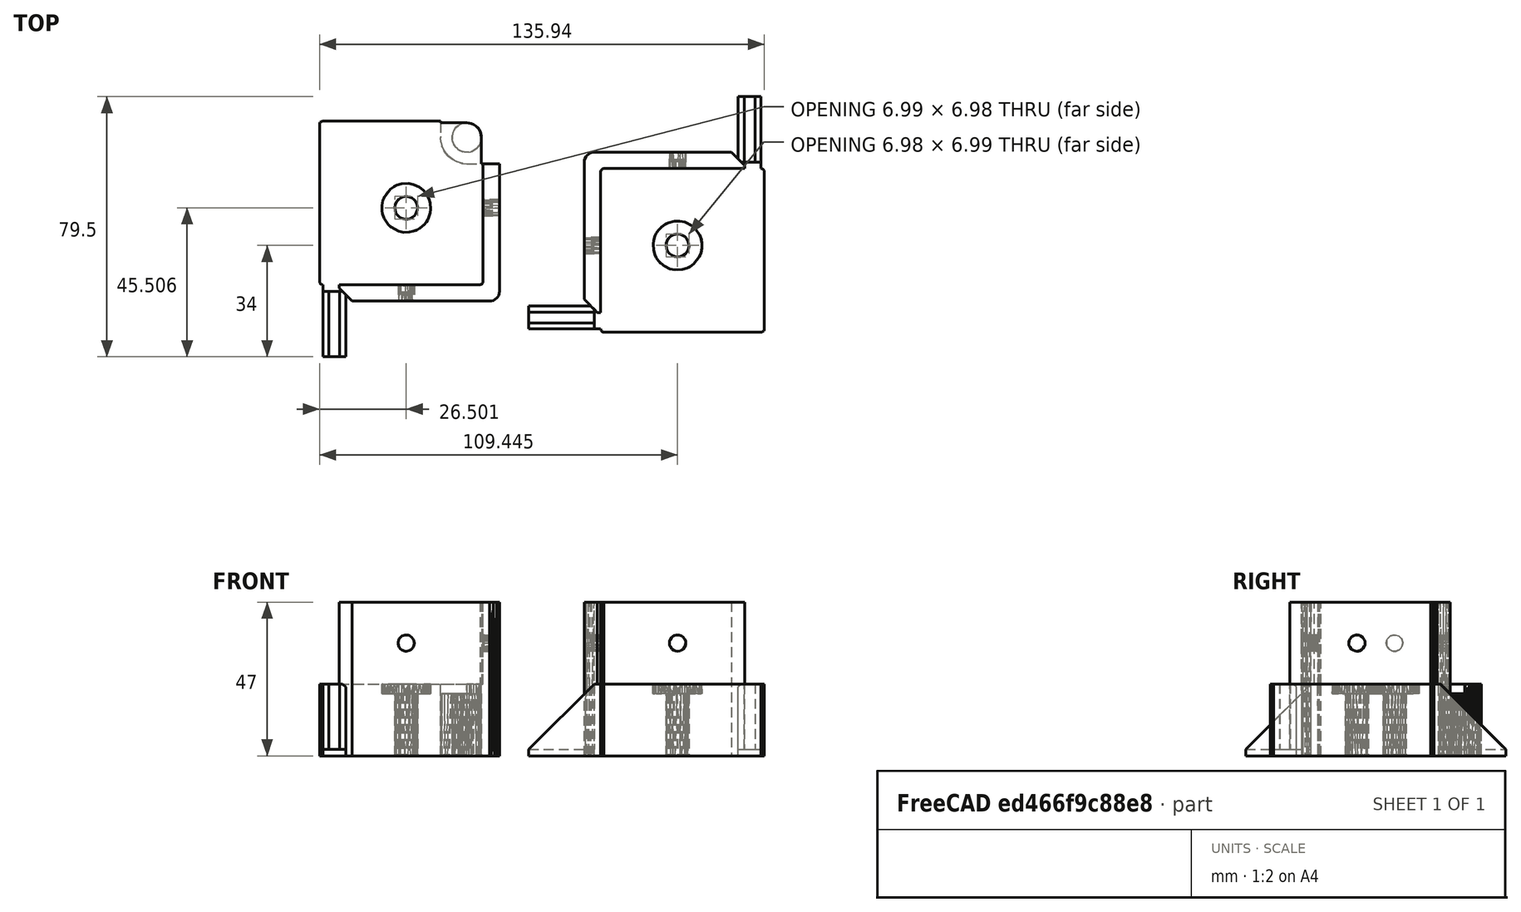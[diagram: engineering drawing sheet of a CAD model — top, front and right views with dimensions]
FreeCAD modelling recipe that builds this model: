
FCSTD DOCUMENT  (FreeCAD 0.18R14555 (Git shallow))
Label: top-holder
License: All rights reserved
LicenseURL: http://en.wikipedia.org/wiki/All_rights_reserved
objects: Part::Box×3, Part::Cut×3, Part::Feature×2
note: 8 computed .brp shape members not serialized (recipe doc carries the construction recipe); baked Part::Feature solids carry a one-line shape summary decoded from their .brp

FEATURE [Part::Feature] top_corner_handle001001_solid  label="top_corner_handle002 (Solid)"
  Placement = pos=(30.38,0.35,0) rot=(0,0,1;0rad)
  shape: bbox 55 x 72 x 47 mm, 346 faces (baked)
FEATURE [Part::Feature] blain_top_corner001001_solid  label="blain_top_corner002 (Solid)"
  Placement = pos=(52.59,0.98,0) rot=(0,0,1;0rad)
  shape: bbox 72 x 72 x 47 mm, 277 faces (baked)
FEATURE [Part::Box] Box  label="Cube"
  AttacherType = Attacher::AttachEngine3D
  Height = 27
  Length = 22
  Placement = pos=(-5.49,-35.73,2) rot=(0,0,1;0rad)
  Width = 3.3
FEATURE [Part::Box] Box001  label="Cube001"
  AttacherType = Attacher::AttachEngine3D
  Height = 27
  Length = 3.3
  Placement = pos=(-64.58,-48.08,2) rot=(0,0,1;0rad)
  Width = 22
FEATURE [Part::Box] Box002  label="Cube002"
  AttacherType = Attacher::AttachEngine3D
  Height = 27
  Length = 3.3
  Placement = pos=(62.36,13.42,2) rot=(0,0,1;0rad)
  Width = 22
FEATURE [Part::Cut] Cut
  Base = -> top_corner_handle001001_solid
  Tool = -> Box001
FEATURE [Part::Cut] Cut001
  Base = -> blain_top_corner001001_solid
  Tool = -> Box002
FEATURE [Part::Cut] Cut002
  Base = -> Cut001
  Tool = -> Box
